# Revit family: Hager-Typ.B_TP&N_IP65_Distribution_Boards-UK-en
name_source: partatom
category: Electrical Equipment
units: mm (PartAtom-declared; Revit-internal decimal feet)

## family parameters
Cut with Voids When Loaded = No
Host = Face
Panel Configuration = Two Columns, Circuits Across
Part Type = Panelboard
Room Calculation Point = No
Round Connector Dimension = Use Diameter
Shared = No

## types (10) — shared parameters
Classification.Uniclass.Pr.Description = Control circuit device enclosures
Classification.Uniclass.Pr.Number = Pr_80_77_28_16
EF000003 - Mounting method = EV000384 - Surface mounted (plaster)
EF000007 - Colour = EV000154 - Other
EF000049 - Depth = 300 mm  [stored 0.984252 ft]
EF000116 - RAL-number = 7035
EF000118 - With mounting plate = No
EF001062 - EMC-version = No
EF001088 - Extension possible = No
EF001134 - DIN-rail = No
EF005474 - Degree of protection (IP) = EV006421 - IP65
EF006244 - Transparent cover/door = No
EF006306 - With lock = Yes
EF015776 - Earthing terminal block = Yes
EF015777 - Neutral terminal block = Yes
EF015941 - Signal passing door = No
HG000002 - With door or cover = Yes
HG000003 - Range = Type B TP&N Distribution Boards
HG000005 - Thickness = 3 mm  [stored 0.00984252 ft]
HG000017 - Distance between poles = 18 mm  [stored 0.0590551 ft]
Manufacturer = Hager
Type Comments = Type B TP&N Distribution Boards
zero-valued in all types: Default Elevation, EF000218 - Built-in depth, EF000266 - Number of rows, EF000332 - Built-in height, EF000846 - Built-in width, EF001131 - Internal depth

## per-type parameters (varying)
| type | EF000008 - Width | EF000040 - Height | EF000339 - Type of cover | EF001596 - Material housing | EF002950 - Width in number of modular spacings | EF004462 - Type of closure | HG000004 - Manufacturer reference | Model |
| Surface mounted IP65 W600 H800 D300 12 Modular spacings - JK108BD | 600 mm  [stored 1.9685 ft] | 800 mm | EV004216 - Door | EV000179 - Steel | 12 | EV000154 - Other | JK108BD | JK108BD |
| Surface mounted IP65 W600 H800 D300 12 Modular spacings - JK108BF | 600 mm  [stored 1.9685 ft] | 800 mm | EV004216 - Door | EV000139 - Plastic | 12 | EV000154 - Other | JK108BF | JK108BF |
| Surface mounted IP65 W600 H800 D300 6 Modular spacings - JK104BD | 600 mm  [stored 1.9685 ft] | 800 mm | EV004216 - Door | EV000179 - Steel | 6 | EV000154 - Other | JK104BD | JK104BD |
| Surface mounted IP65 W600 H800 D300 6 Modular spacings - JK104BF | 600 mm  [stored 1.9685 ft] | 800 mm | EV004216 - Door | EV000139 - Plastic | 6 | EV000154 - Other | JK104BF | JK104BF |
| Surface mounted IP65 W600 H800 D300 9 Modular spacings - JK106BD | 600 mm  [stored 1.9685 ft] | 800 mm | EV001012 - Cover | EV000179 - Steel | 9 | EV000154 - Other | JK106BD | JK106BD |
| Surface mounted IP65 W600 H800 D300 9 Modular spacings - JK106BF | 600 mm  [stored 1.9685 ft] | 800 mm | EV004216 - Door | EV000139 - Plastic | 9 | EV001412 - Cylinder | JK106BF | JK106BF |
| Surface mounted IP65 W850 H1250 D300 18 Modular spacings - JK112BF | 850 mm  [stored 2.78871 ft] | 1250 mm  [stored 4.10105 ft] | EV004216 - Door | EV000139 - Plastic | 18 | EV000154 - Other | JK112BF | JK112BF |
| Surface mounted IP65 W850 H1250 D300 24 Modular spacings - JK116BF | 850 mm  [stored 2.78871 ft] | 1250 mm  [stored 4.10105 ft] | EV004216 - Door | EV000139 - Plastic | 24 | EV000154 - Other | JK116BF | JK116BF |
| Surface mounted IP65 W850 H950 D300 18 Modular spacings - JK112BD | 850 mm  [stored 2.78871 ft] | 950 mm  [stored 3.1168 ft] | EV004216 - Door | EV000179 - Steel | 18 | EV000154 - Other | JK112BD | JK112BD |
| Surface mounted IP65 W850 H950 D300 24 Modular spacings - JK116BD | 850 mm  [stored 2.78871 ft] | 950 mm  [stored 3.1168 ft] | EV004216 - Door | EV000179 - Steel | 24 | EV000154 - Other | JK116BD | JK116BD |

note: [stored X ft] marks values corroborated as IEEE doubles in the binary element streams (Revit-internal decimal feet)

## geometry (parser evidence)
native form markers: Sweep x8
no freeform markers — native parametric forms only
